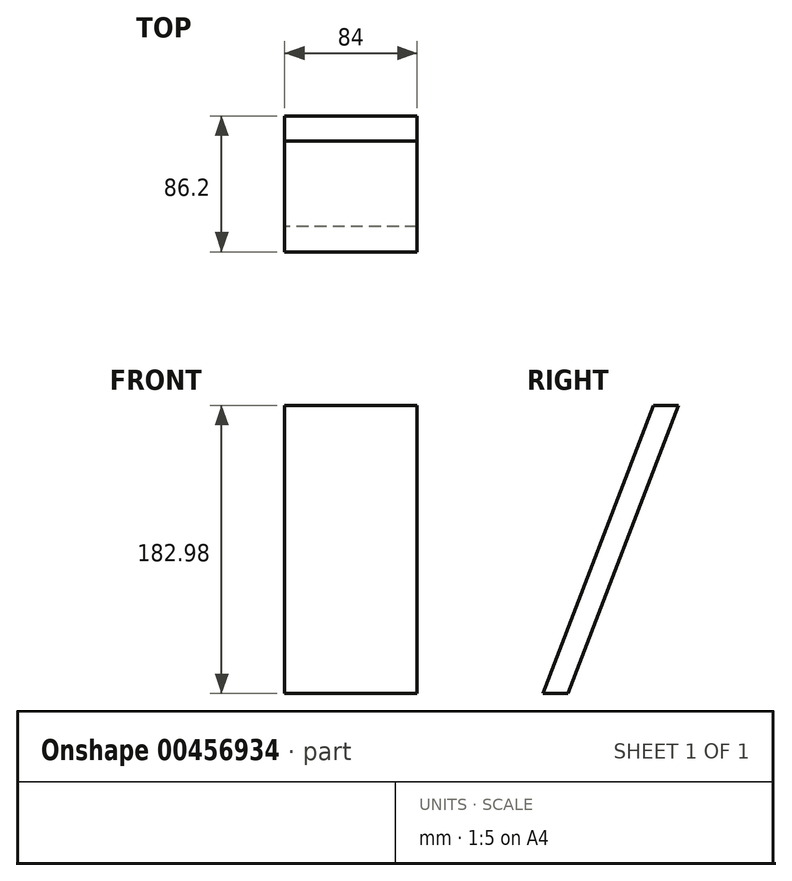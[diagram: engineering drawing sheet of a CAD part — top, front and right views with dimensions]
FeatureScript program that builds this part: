
annotation { "Feature Type Name" : "Feature", "Feature Type Description" : "" }
export const myFeature = defineFeature(function(context is Context, id is Id, definition is map)
    precondition{}
    {
        {
            assignVariable(context, id + "F0", {"name" : "PhoneWidth", "anyValue" : 84});
        }
        {
            var Q0;
            Q0=qCreatedBy(makeId("Right.planeOp"),FACE);
            var sketch = newSketch(context, id + "F1", { "sketchPlane" : qUnion([Q0])});
            skLineSegment(sketch, "E0", {"start": v(0, 182.98) * mm, "end": v(-15.96, 182.98) * mm});
            skLineSegment(sketch, "E1", {"start": v(-15.96, 182.98) * mm, "end": v(-86.2, 0) * mm});
            skLineSegment(sketch, "E2", {"start": v(-86.2, 0) * mm, "end": v(-70.24, 0) * mm});
            skLineSegment(sketch, "E3", {"start": v(-70.24, 0) * mm, "end": v(0, 182.98) * mm});
            skLineSegment(sketch, "E4", {"start": v(0, 0) * mm, "end": v(-35.75, 0) * mm});
            skLineSegment(sketch, "E5", {"start": v(-35.75, 0) * mm, "end": v(-90.47, 25.09) * mm});
            skLineSegment(sketch, "E6", {"start": v(-90.47, 25.09) * mm, "end": v(-85.12, 39.03) * mm});
            skLineSegment(sketch, "E7", {"start": v(-85.12, 39.03) * mm, "end": v(0, 0) * mm});
            skLineSegment(sketch, "E8", {"start": v(-35.75, 0) * mm, "end": v(-29.54, 13.54) * mm, "construction": true});
            skLineSegment(sketch, "E9", {"start": v(0, 0) * mm, "end": v(0, 182.98) * mm, "construction": true});
            skLineSegment(sketch, "E10", {"start": v(-85.12, 39.03) * mm, "end": v(-73.3, 33.6) * mm, "construction": true});
            skLineSegment(sketch, "E11", {"start": v(-15.96, 182.98) * mm, "end": v(-73.3, 33.6) * mm, "construction": true});
            skLineSegment(sketch, "E12", {"start": v(-73.3, 33.6) * mm, "end": v(-86.2, 0) * mm, "construction": true});
            skLineSegment(sketch, "E13", {"start": v(-15.96, 182.98) * mm, "end": v(-2.05, 177.64) * mm, "construction": true});
            skLineSegment(sketch, "E14", {"start": v(0, 182.98) * mm, "end": v(-13.91, 188.32) * mm, "construction": true});
            skLineSegment(sketch, "E15", {"start": v(-86.2, 0) * mm, "end": v(-13.91, 188.32) * mm, "construction": true});
            skLineSegment(sketch, "E16", {"start": v(-85.12, 39.03) * mm, "end": v(-59.73, 27.39) * mm, "construction": true});
            skSolve(sketch);
        }
        {
            var Q0;
            {var subQ0=sQuery(id+"F1.wireOp",EDGE,"E0");Q0=makeQuery(id+"F1.imprint","IMPRINT",FACE,{"disambiguationData":[TD([[makeQuery(id+"F1.imprint","IMPRINT",EDGE,{"derivedFrom":subQ0}),1.0]])]});}
            var Q1;
            {var subQ0=sQuery(id+"F1.wireOp",EDGE,"E7");var subQ1=sQuery(id+"F1.wireOp",EDGE,"E1");var subQ2=makeQuery(id+"F1.imprint","INTERSECT",VERTEX,{"derivedFrom":[subQ1,subQ0]});Q1=makeQuery(id+"F1.imprint","IMPRINT",FACE,{"disambiguationData":[TD([[makeQuery(id+"F1.imprint","IMPRINT",EDGE,{"disambiguationData":[TD([[subQ2,-1.0]])],"derivedFrom":subQ1}),1.0]])]});}
            var Q2;
            {var subQ0=sQuery(id+"F1.wireOp",EDGE,"E2");Q2=makeQuery(id+"F1.imprint","IMPRINT",FACE,{"disambiguationData":[TD([[makeQuery(id+"F1.imprint","IMPRINT",EDGE,{"derivedFrom":subQ0}),1.0]])]});}
            extrude(context, id + "F2", {"entities" : qUnion([Q0, Q1, Q2]), "depth" : (getVariable(context, 'PhoneWidth')) * mm});
        }
    });
